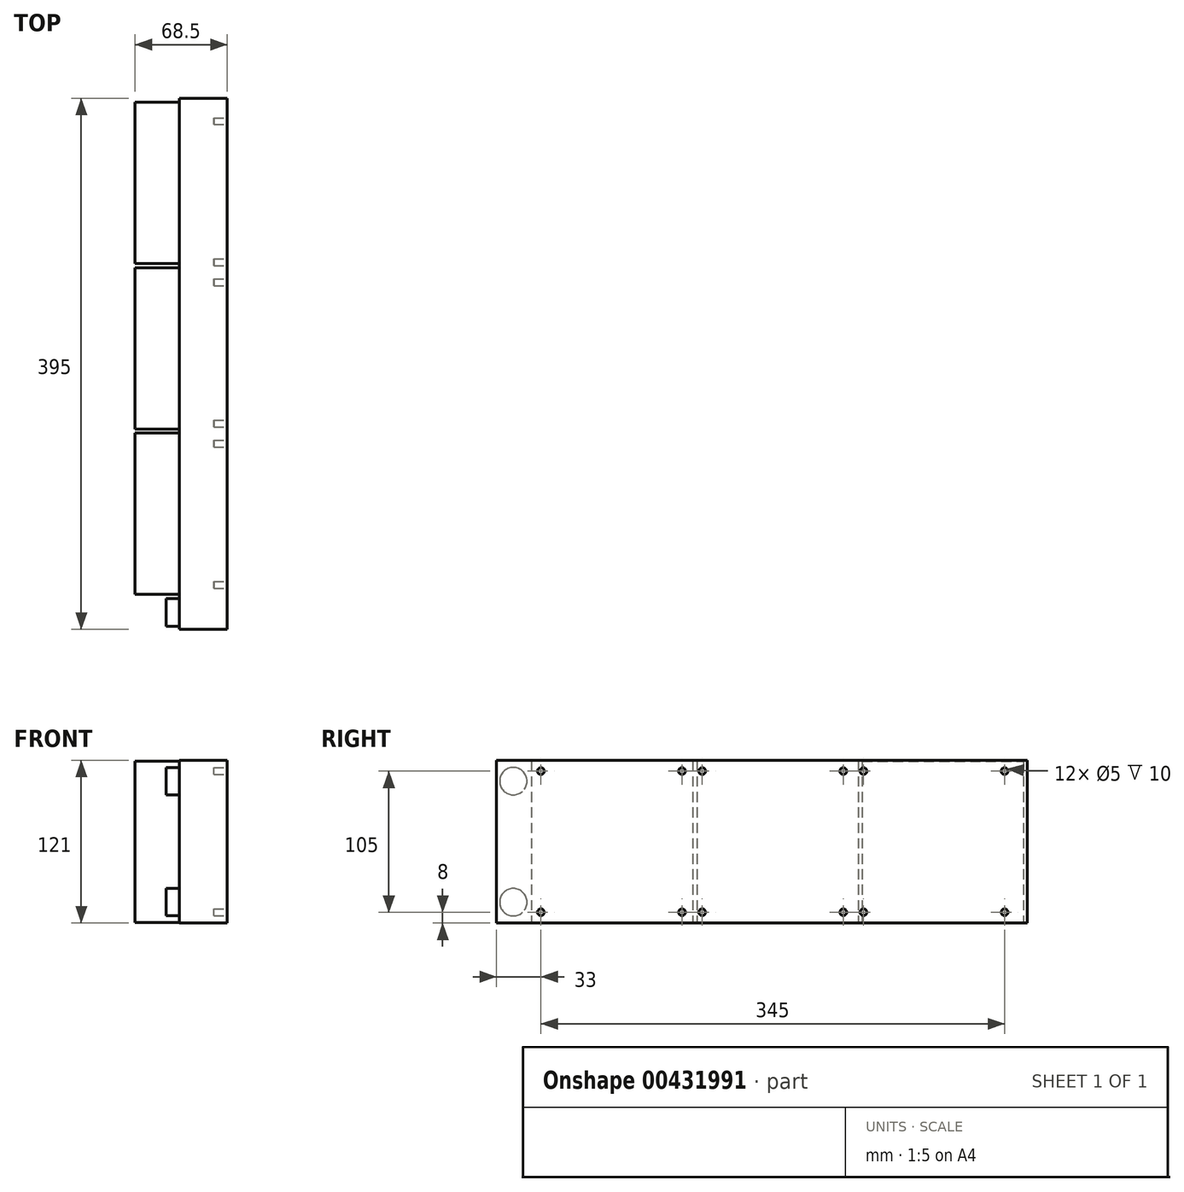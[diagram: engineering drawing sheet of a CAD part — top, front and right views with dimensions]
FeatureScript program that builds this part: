
annotation { "Feature Type Name" : "Feature", "Feature Type Description" : "" }
export const myFeature = defineFeature(function(context is Context, id is Id, definition is map)
    precondition{}
    {
        {
            var Q0;
            Q0=qCreatedBy(makeId("Right.planeOp"),FACE);
            var sketch = newSketch(context, id + "F0", { "sketchPlane" : qUnion([Q0])});
            skLineSegment(sketch, "E0.bottom", {"start": v(197.5, 60.5) * mm, "end": v(-197.5, 60.5) * mm});
            skLineSegment(sketch, "E0.top", {"start": v(197.5, -60.5) * mm, "end": v(-197.5, -60.5) * mm});
            skLineSegment(sketch, "E0.left", {"start": v(197.5, 60.5) * mm, "end": v(197.5, -60.5) * mm});
            skLineSegment(sketch, "E0.right", {"start": v(-197.5, 60.5) * mm, "end": v(-197.5, -60.5) * mm});
            skPoint(sketch, "E0.middle", {"position": v(0, 0) * mm});
            skSolve(sketch);
        }
        {
            var Q0;
            Q0=qSketchRegion(id+"F0",true);
            extrude(context, id + "F1", {"entities" : qUnion([Q0]), "depth" : 35.5 * mm});
        }
        {
            var Q0;
            Q0=makeQuery(id+"F1.opExtrude","CAP_FACE",FACE,{"disambiguationData":[OSD([sQuery(id+"F0.wireOp",EDGE,"E0.bottom"),sQuery(id+"F0.wireOp",EDGE,"E0.top"),sQuery(id+"F0.wireOp",EDGE,"E0.left"),sQuery(id+"F0.wireOp",EDGE,"E0.right")])],"isStart":true});
            var sketch = newSketch(context, id + "F2", { "sketchPlane" : qUnion([Q0])});
            skLineSegment(sketch, "E1", {"start": v(-197.5, 0) * mm, "end": v(197.5, 0) * mm, "construction": true});
            skLineSegment(sketch, "E2.bottom", {"start": v(-74.5, 60) * mm, "end": v(-194.5, 60) * mm});
            skLineSegment(sketch, "E2.top", {"start": v(-74.5, -60) * mm, "end": v(-194.5, -60) * mm});
            skLineSegment(sketch, "E2.left", {"start": v(-74.5, 60) * mm, "end": v(-74.5, -60) * mm});
            skLineSegment(sketch, "E2.right", {"start": v(-194.5, 60) * mm, "end": v(-194.5, -60) * mm});
            skPoint(sketch, "E2.middle", {"position": v(-134.5, 0) * mm});
            skLineSegment(sketch, "E3.bottom", {"start": v(-71.5, 60) * mm, "end": v(48.5, 60) * mm});
            skLineSegment(sketch, "E3.top", {"start": v(-71.5, -60) * mm, "end": v(48.5, -60) * mm});
            skLineSegment(sketch, "E3.left", {"start": v(-71.5, 60) * mm, "end": v(-71.5, -60) * mm});
            skLineSegment(sketch, "E3.right", {"start": v(48.5, 60) * mm, "end": v(48.5, -60) * mm});
            skPoint(sketch, "E3.middle", {"position": v(-11.5, 0) * mm});
            skPoint(sketch, "E3.cornerSnap0", {"position": v(-71.5, 60.5) * mm});
            skLineSegment(sketch, "E4.bottom", {"start": v(51.5, 60) * mm, "end": v(171.5, 60) * mm});
            skLineSegment(sketch, "E4.top", {"start": v(51.5, -60) * mm, "end": v(171.5, -60) * mm});
            skLineSegment(sketch, "E4.left", {"start": v(51.5, 60) * mm, "end": v(51.5, -60) * mm});
            skLineSegment(sketch, "E4.right", {"start": v(171.5, 60) * mm, "end": v(171.5, -60) * mm});
            skPoint(sketch, "E4.middle", {"position": v(111.5, 0) * mm});
            skSolve(sketch);
        }
        {
            var Q0;
            Q0=qSketchRegion(id+"F2",true);
            extrude(context, id + "F3", {"entities" : qUnion([Q0]), "operationType" : NewBodyOperationType.ADD, "depth" : 33 * mm});
        }
        {
            var Q0;
            Q0=makeQuery(id+"F1.opExtrude","CAP_FACE",FACE,{"disambiguationData":[OSD([sQuery(id+"F0.wireOp",EDGE,"E0.bottom"),sQuery(id+"F0.wireOp",EDGE,"E0.top"),sQuery(id+"F0.wireOp",EDGE,"E0.left"),sQuery(id+"F0.wireOp",EDGE,"E0.right")])],"isStart":true});
            var sketch = newSketch(context, id + "F4", { "sketchPlane" : qUnion([Q0])});
            skCircle(sketch, "E5", {"center": v(185, 45) * mm, "radius": 10.2 * mm});
            skLineSegment(sketch, "E6", {"start": v(185, 60.5) * mm, "end": v(185, -60.5) * mm, "construction": true});
            skLineSegment(sketch, "E7", {"start": v(197.5, 0) * mm, "end": v(185, 0) * mm, "construction": true});
            skCircle(sketch, "E8.MirrorC", {"center": v(185, -45) * mm, "radius": 10.2 * mm});
            skSolve(sketch);
        }
        {
            var Q0;
            Q0=qSketchRegion(id+"F4",true);
            extrude(context, id + "F5", {"entities" : qUnion([Q0]), "operationType" : NewBodyOperationType.ADD, "depth" : 10 * mm});
        }
        {
            var Q0;
            Q0=makeQuery(id+"F1.opExtrude","CAP_FACE",FACE,{"disambiguationData":[OSD([sQuery(id+"F0.wireOp",EDGE,"E0.bottom"),sQuery(id+"F0.wireOp",EDGE,"E0.top"),sQuery(id+"F0.wireOp",EDGE,"E0.left"),sQuery(id+"F0.wireOp",EDGE,"E0.right")])],"isStart":false});
            var sketch = newSketch(context, id + "F6", { "sketchPlane" : qUnion([Q0])});
            skCircle(sketch, "E9", {"center": v(180.5, -52.5) * mm, "radius": 2.5 * mm});
            skCircle(sketch, "E10", {"center": v(75.5, -52.5) * mm, "radius": 2.5 * mm});
            skCircle(sketch, "E11", {"center": v(60.5, -52.5) * mm, "radius": 2.5 * mm});
            skLineSegment(sketch, "E12", {"start": v(8, -60.5) * mm, "end": v(8, 60.5) * mm, "construction": true});
            skLineSegment(sketch, "E13", {"start": v(8, 0) * mm, "end": v(197.5, 0) * mm, "construction": true});
            skCircle(sketch, "E14.MirrorC", {"center": v(180.5, 52.5) * mm, "radius": 2.5 * mm});
            skCircle(sketch, "E15.MirrorC", {"center": v(75.5, 52.5) * mm, "radius": 2.5 * mm});
            skCircle(sketch, "E16.MirrorC", {"center": v(60.5, 52.5) * mm, "radius": 2.5 * mm});
            skCircle(sketch, "E17.MirrorC", {"center": v(-44.5, 52.5) * mm, "radius": 2.5 * mm});
            skCircle(sketch, "E18.MirrorC", {"center": v(-59.5, 52.5) * mm, "radius": 2.5 * mm});
            skCircle(sketch, "E19.MirrorC", {"center": v(-164.5, 52.5) * mm, "radius": 2.5 * mm});
            skCircle(sketch, "E20.MirrorC", {"center": v(-44.5, -52.5) * mm, "radius": 2.5 * mm});
            skCircle(sketch, "E21.MirrorC", {"center": v(-164.5, -52.5) * mm, "radius": 2.5 * mm});
            skCircle(sketch, "E22.MirrorC", {"center": v(-59.5, -52.5) * mm, "radius": 2.5 * mm});
            skSolve(sketch);
        }
        {
            var Q0;
            Q0 = qSketchRegion(id + "F6", true);
            extrude(context, id + "F7", {"entities" : qUnion([Q0]), "operationType" : NewBodyOperationType.REMOVE, "oppositeDirection" : true, "depth" : 10 * mm});
        }
    });
